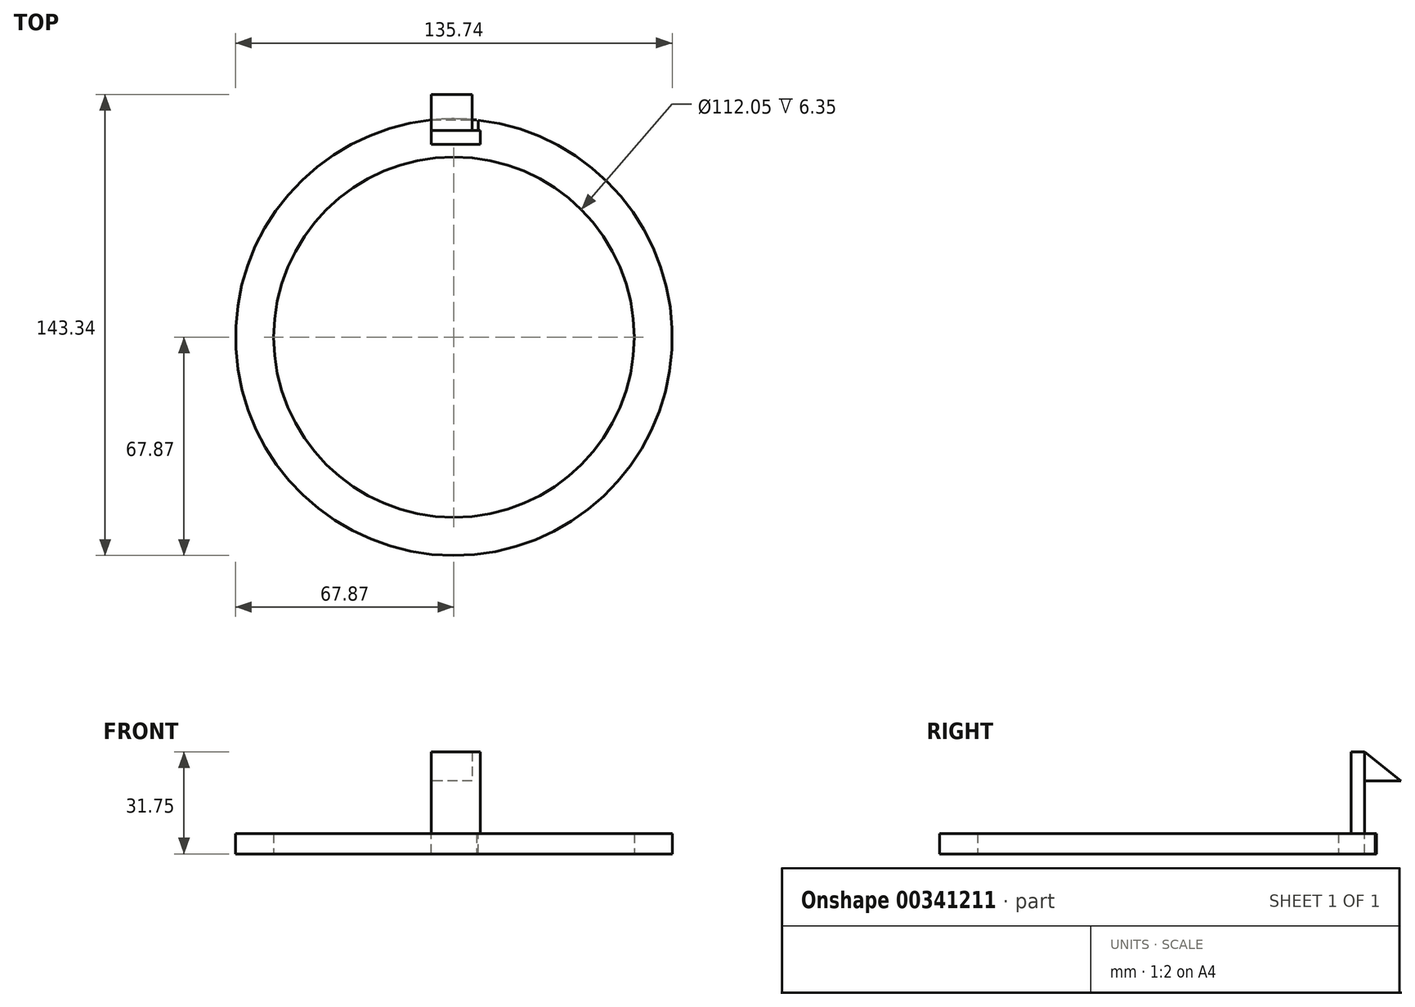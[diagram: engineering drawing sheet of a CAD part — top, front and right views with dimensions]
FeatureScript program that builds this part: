
annotation { "Feature Type Name" : "Feature", "Feature Type Description" : "" }
export const myFeature = defineFeature(function(context is Context, id is Id, definition is map)
    precondition{}
    {
        {
            var Q0;
            Q0=qCreatedBy(makeId("Top.planeOp"),FACE);
            var sketch = newSketch(context, id + "F0", { "sketchPlane" : qUnion([Q0])});
            skCircle(sketch, "E0", {"center": v(0, 0) * mm, "radius": 67.87 * mm});
            skSolve(sketch);
        }
        {
            var Q0;
            Q0=makeQuery(id+"F0.imprint","IMPRINT",FACE,{"disambiguationData":[TD([[makeQuery(id+"F0.imprint","IMPRINT",EDGE,{"derivedFrom":sQuery(id+"F0.wireOp",EDGE,"E0")}),1.0]])]});
            extrude(context, id + "F1", {"entities" : qUnion([Q0]), "depth" : 6.35 * mm});
        }
        {
            var Q0;
            Q0=qCreatedBy(makeId("Top.planeOp"),FACE);
            var sketch = newSketch(context, id + "F2", { "sketchPlane" : qUnion([Q0])});
            skCircle(sketch, "E1", {"center": v(0, 0) * mm, "radius": 56.03 * mm});
            skSolve(sketch);
        }
        {
            var Q0;
            Q0=makeQuery(id+"F2.imprint","IMPRINT",FACE,{"disambiguationData":[TD([[makeQuery(id+"F2.imprint","IMPRINT",EDGE,{"derivedFrom":sQuery(id+"F2.wireOp",EDGE,"E1")}),1.0]])]});
            var Q1;
            Q1=sQuery(id+"F2.wireOp",EDGE,"E1");
            extrude(context, id + "F3", {"entities" : qUnion([Q0]), "operationType" : NewBodyOperationType.REMOVE, "surfaceEntities" : qUnion([Q1]), "depth" : 19.05 * mm});
        }
        {
            var Q0;
            Q0=makeQuery(id+"F1.opExtrude","CAP_FACE",FACE,{"disambiguationData":[OSD([sQuery(id+"F0.wireOp",EDGE,"E0")])],"isStart":false});
            var sketch = newSketch(context, id + "F4", { "sketchPlane" : qUnion([Q0])});
            skLineSegment(sketch, "E2.bottom", {"start": v(-7.05, 67.5) * mm, "end": v(7.52, 67.5) * mm});
            skLineSegment(sketch, "E2.top", {"start": v(-7.05, 64.26) * mm, "end": v(7.52, 64.26) * mm});
            skLineSegment(sketch, "E2.left", {"start": v(-7.05, 67.5) * mm, "end": v(-7.05, 64.26) * mm});
            skLineSegment(sketch, "E2.right", {"start": v(7.52, 67.5) * mm, "end": v(7.52, 64.26) * mm});
            skSolve(sketch);
        }
        {
            var Q0;
            Q0 = qSketchRegion(id + "F4", true);
            extrude(context, id + "F5", {"entities" : qUnion([Q0]), "operationType" : NewBodyOperationType.REMOVE, "oppositeDirection" : true, "depth" : 6.35 * mm});
        }
        {
            var Q0;
            {var subQ0=sQuery(id+"F0.wireOp",EDGE,"E0");Q0=makeQuery(id+"F5.boolean.opBoolean","SPLIT",FACE,{"disambiguationData":[TD([makeQuery(id+"F3.boolean.opBoolean","COPY",FACE,{"derivedFrom":makeQuery(id+"F3.opExtrude","SWEPT_FACE",FACE,{"disambiguationData":[OSD([sQuery(id+"F2.wireOp",EDGE,"E1")])]})})])],"derivedFrom":makeQuery(id+"F1.opExtrude","CAP_FACE",FACE,{"disambiguationData":[OSD([subQ0])],"isStart":false})});}
            var sketch = newSketch(context, id + "F6", { "sketchPlane" : qUnion([Q0])});
            skLineSegment(sketch, "E3.bottom", {"start": v(-7.05, 64.26) * mm, "end": v(8.23, 64.26) * mm});
            skLineSegment(sketch, "E3.top", {"start": v(-7.05, 59.96) * mm, "end": v(8.23, 59.96) * mm});
            skLineSegment(sketch, "E3.left", {"start": v(-7.05, 64.26) * mm, "end": v(-7.05, 59.96) * mm});
            skLineSegment(sketch, "E3.right", {"start": v(8.23, 64.26) * mm, "end": v(8.23, 59.96) * mm});
            skSolve(sketch);
        }
        {
            var Q0;
            Q0 = qSketchRegion(id + "F6", true);
            extrude(context, id + "F7", {"entities" : qUnion([Q0]), "operationType" : NewBodyOperationType.ADD, "depth" : 25.4 * mm});
        }
        {
            var Q0;
            Q0=makeQuery(id+"F7.opExtrude","SWEPT_FACE",FACE,{"disambiguationData":[OSD([sQuery(id+"F6.wireOp",EDGE,"E3.left")])]});
            var sketch = newSketch(context, id + "F8", { "sketchPlane" : qUnion([Q0])});
            skLineSegment(sketch, "E4", {"start": v(-64.26, 22.69) * mm, "end": v(-75.47, 22.69) * mm});
            skLineSegment(sketch, "E5", {"start": v(-75.47, 22.69) * mm, "end": v(-64.26, 31.75) * mm});
            skLineSegment(sketch, "E6", {"start": v(-64.26, 31.75) * mm, "end": v(-64.26, 22.69) * mm});
            skSolve(sketch);
        }
        {
            var Q0;
            Q0 = qSketchRegion(id + "F8", true);
            extrude(context, id + "F9", {"entities" : qUnion([Q0]), "operationType" : NewBodyOperationType.ADD, "depth" : -12.7 * mm});
        }
    });
